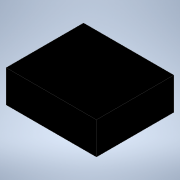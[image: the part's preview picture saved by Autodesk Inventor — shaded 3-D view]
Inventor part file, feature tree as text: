
AUTODESK INVENTOR PART (.ipt)
format: ipt  version: 2020 (Build 240168000, 168)  size: 91,136 bytes
history: native  units: mm
features: other x1, extrude x1, sketch x1
ambient origin geometry x8: Origin, YZ Plane, XZ Plane, XY Plane, X Axis, Y Axis, Z Axis, Center Point
bodies: Body1 (feature_tree)
feature tree (3):
  other  "Sólido1"
  extrude  "Extrusão1"  Depth=25.0mm
  sketch  "Esboço1"  dims[d0=70.0mm d1=25.0mm d2=60.0mm d3=0.0mm]
